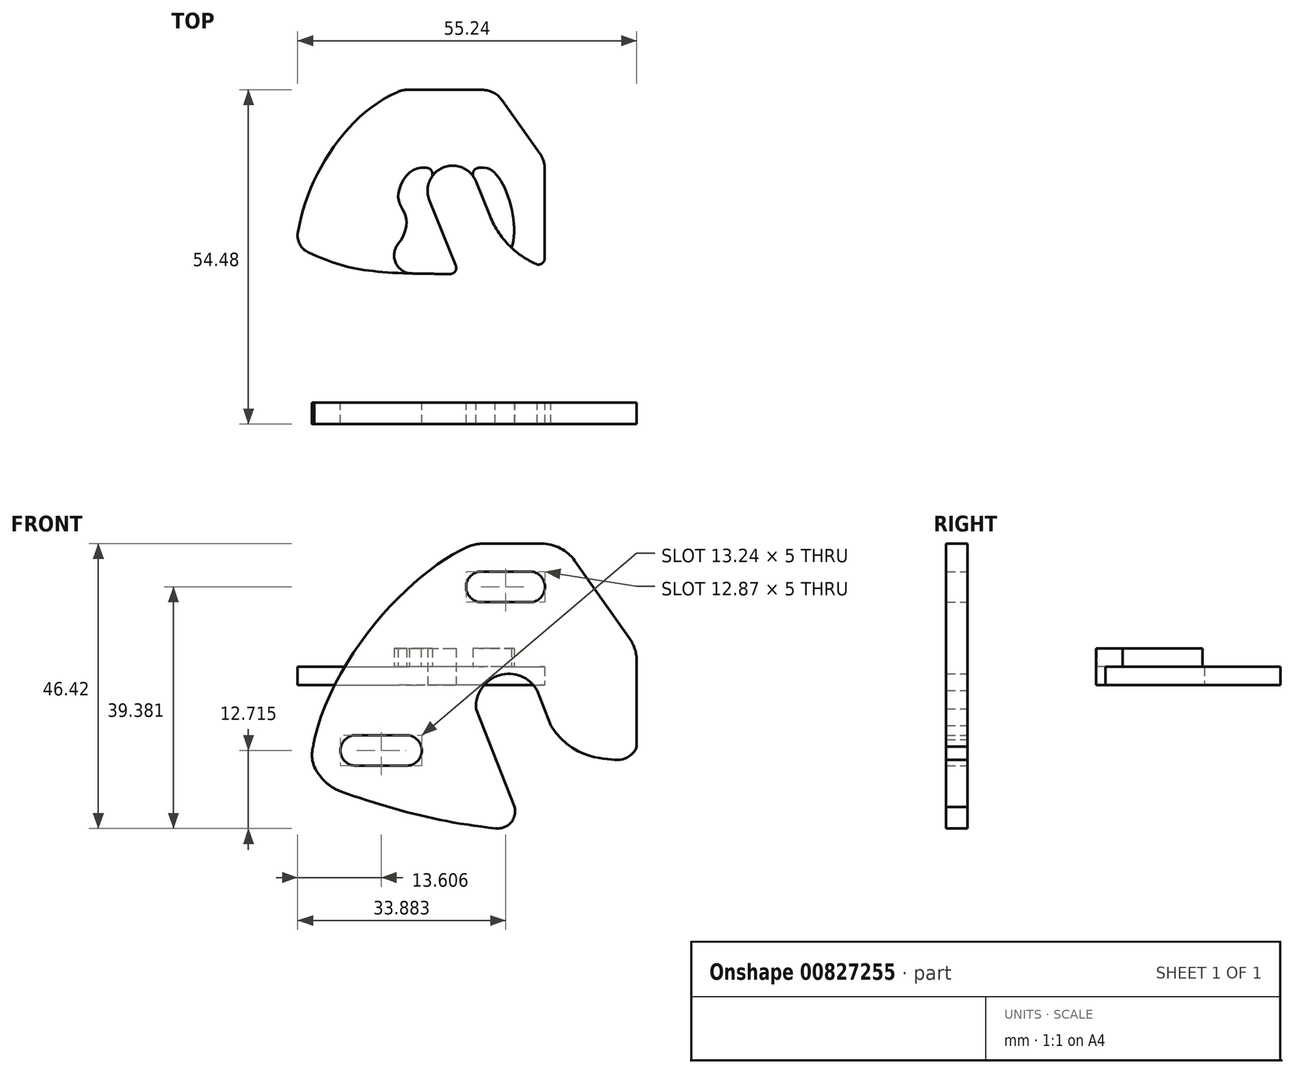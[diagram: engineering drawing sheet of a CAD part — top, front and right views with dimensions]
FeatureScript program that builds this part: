
annotation { "Feature Type Name" : "Feature", "Feature Type Description" : "" }
export const myFeature = defineFeature(function(context is Context, id is Id, definition is map)
    precondition{}
    {
        {
            var Q0;
            Q0=qCreatedBy(makeId("Top.planeOp"),FACE);
            var sketch = newSketch(context, id + "F0", { "sketchPlane" : qUnion([Q0])});
            skLineSegment(sketch, "E0", {"start": v(4.25, 49.3) * mm, "end": v(10.45, 40.56) * mm});
            skLineSegment(sketch, "E1", {"start": v(11.2, 22.02) * mm, "end": v(11.2, 38.24) * mm});
            skLineSegment(sketch, "E2", {"start": v(-7.58, 33) * mm, "end": v(-2.72, 20.95) * mm});
            skLineSegment(sketch, "E3", {"start": v(1, 50.98) * mm, "end": v(-11.14, 50.98) * mm});
            skLineSegment(sketch, "E4", {"start": v(2.27, 30.41) * mm, "end": v(0, 36.06) * mm});
            skFitSpline(sketch, "E5", {"points": [v(-29.3, 25.47) * mm, v(-11.94, 50.98) * mm], "startDerivative": vector(2.86, 30.39) * mm, "endDerivative": vector(29.4, 11.58) * mm});
            skFitSpline(sketch, "E6", {"points": [v(-29.3, 25.47) * mm, v(-2.72, 20.95) * mm], "startDerivative": vector(25.14, -12.86) * mm, "endDerivative": vector(43.82, -0.3) * mm});
            skArc(sketch, "E7", {"start": v(0, 36.06) * mm, "mid": v(-5.32, 38.32) * mm, "end": v(-7.58, 33) * mm});
            skArc(sketch, "E8", {"start": v(2.27, 30.41) * mm, "mid": v(5.81, 25.24) * mm, "end": v(11.2, 22.02) * mm});
            skLineSegment(sketch, "E9", {"start": v(-2.13, 38.26) * mm, "end": v(1.37, 38.26) * mm});
            skFitSpline(sketch, "E10", {"points": [v(5.81, 25.24) * mm, v(1.37, 38.26) * mm], "startDerivative": vector(4.46, 12.1) * mm, "endDerivative": vector(-9.6, 0) * mm});
            skLineSegment(sketch, "E11", {"start": v(-5.45, 38.26) * mm, "end": v(-8.94, 38.26) * mm});
            skFitSpline(sketch, "E12", {"points": [v(-8.94, 38.26) * mm, v(-12.66, 33.83) * mm, v(-11.42, 30.22) * mm, v(-12.66, 25.88) * mm], "startDerivative": vector(-14.89, 0.92) * mm, "endDerivative": vector(-9.91, -12.18) * mm});
            skArc(sketch, "E13", {"start": v(-12.66, 25.88) * mm, "mid": v(-12.95, 22.55) * mm, "end": v(-9.97, 21.04) * mm});
            skPoint(sketch, "E14.visualSharp", {"position": v(11.2, 39.52) * mm});
            skArc(sketch, "E14.filletArc", {"start": v(11.2, 38.24) * mm, "mid": v(11, 39.46) * mm, "end": v(10.45, 40.56) * mm});
            skPoint(sketch, "E15.visualSharp", {"position": v(3.06, 50.98) * mm});
            skArc(sketch, "E15.filletArc", {"start": v(4.25, 49.3) * mm, "mid": v(2.83, 50.53) * mm, "end": v(1, 50.98) * mm});
            skArc(sketch, "E16.filletArc", {"start": v(-11.14, 50.98) * mm, "mid": v(-11.97, 50.89) * mm, "end": v(-12.77, 50.63) * mm});
            skArc(sketch, "E17.filletArc", {"start": v(-29, 27.72) * mm, "mid": v(-28.71, 25.83) * mm, "end": v(-27.33, 24.5) * mm});
            skSolve(sketch);
        }
        {
            var Q0;
            Q0=makeQuery(id+"F0.imprint","IMPRINT",FACE,{"disambiguationData":[TD([[makeQuery(id+"F0.imprint","IMPRINT",EDGE,{"derivedFrom":sQuery(id+"F0.wireOp",EDGE,"E0")}),-1.0]])]});
            extrude(context, id + "F1", {"entities" : qUnion([Q0]), "depth" : 3 * mm, "offsetDistance" : 25 * mm});
        }
        {
            var Q0;
            {var subQ1=sQuery(id+"F0.wireOp",EDGE,"E2");Q0=makeQuery(id+"F0.imprint","IMPRINT",FACE,{"disambiguationData":[TD([[makeQuery(id+"F0.imprint","IMPRINT",EDGE,{"derivedFrom":subQ1}),-1.0]])]});}
            var Q1;
            {var subQ1=sQuery(id+"F0.wireOp",EDGE,"E4");Q1=makeQuery(id+"F0.imprint","IMPRINT",FACE,{"disambiguationData":[TD([[makeQuery(id+"F0.imprint","IMPRINT",EDGE,{"derivedFrom":subQ1}),-1.0]])]});}
            extrude(context, id + "F2", {"entities" : qUnion([Q0, Q1]), "operationType" : NewBodyOperationType.ADD, "depth" : 6 * mm, "offsetDistance" : 25 * mm});
        }
        {
            var Q0;
            Q0=makeQuery(id+"F2.opExtrude","SWEPT_EDGE",EDGE,{"disambiguationData":[OSD([sQuery(id+"F0.wireOp",EDGE,"E7"),sQuery(id+"F0.wireOp",EDGE,"E9")])]});
            var Q1;
            Q1=makeQuery(id+"F2.opExtrude","SWEPT_EDGE",EDGE,{"disambiguationData":[OSD([sQuery(id+"F0.wireOp",EDGE,"E7"),sQuery(id+"F0.wireOp",EDGE,"E11")])]});
            var Q2;
            Q2=makeQuery(id+"F1.opExtrude","SWEPT_EDGE",EDGE,{"disambiguationData":[OSD([sQuery(id+"F0.wireOp",EDGE,"E1"),sQuery(id+"F0.wireOp",EDGE,"E8")])]});
            var Q3;
            Q3=makeQuery(id+"F2.opExtrude","SWEPT_EDGE",EDGE,{"disambiguationData":[OSD([sQuery(id+"F0.wireOp",EDGE,"E2"),sQuery(id+"F0.wireOp",EDGE,"E6")])]});
            fillet(context, id + "F3", {"entities" : qUnion([Q0, Q1, Q2, Q3]), "radius" : 1 * mm, "tangentPropagation" : true, "allowEdgeOverflow" : false});
        }
        {
            var Q0;
            Q0=qCreatedBy(makeId("Front.planeOp"),FACE);
            var sketch = newSketch(context, id + "F4", { "sketchPlane" : qUnion([Q0])});
            skLineSegment(sketch, "E18", {"start": v(0, 23.06) * mm, "end": v(14.14, 23.06) * mm});
            skLineSegment(sketch, "E19", {"start": v(14.14, 23.06) * mm, "end": v(26.2, 6) * mm});
            skLineSegment(sketch, "E20", {"start": v(26.2, 6) * mm, "end": v(26.2, -10.04) * mm});
            skLineSegment(sketch, "E21", {"start": v(0.9, 18.52) * mm, "end": v(8.77, 18.52) * mm});
            skLineSegment(sketch, "E22", {"start": v(0.9, 13.52) * mm, "end": v(8.77, 13.52) * mm});
            skLineSegment(sketch, "E23", {"start": v(-19.56, -8.15) * mm, "end": v(-11.32, -8.15) * mm});
            skLineSegment(sketch, "E24", {"start": v(-19.56, -13.15) * mm, "end": v(-11.32, -13.15) * mm});
            skArc(sketch, "E25", {"start": v(-11.32, -8.15) * mm, "mid": v(-8.82, -10.65) * mm, "end": v(-11.32, -13.15) * mm});
            skArc(sketch, "E26", {"start": v(-19.56, -8.15) * mm, "mid": v(-22.06, -10.65) * mm, "end": v(-19.56, -13.15) * mm});
            skArc(sketch, "E27", {"start": v(8.77, 13.52) * mm, "mid": v(11.27, 16.02) * mm, "end": v(8.77, 18.52) * mm});
            skArc(sketch, "E28", {"start": v(0.9, 18.52) * mm, "mid": v(-1.6, 16.02) * mm, "end": v(0.9, 13.52) * mm});
            skArc(sketch, "E29", {"start": v(10, -0.85) * mm, "mid": v(3.8, 1.6) * mm, "end": v(0, -3.87) * mm});
            skLineSegment(sketch, "E30", {"start": v(10, -0.85) * mm, "end": v(12.21, -6.6) * mm});
            skLineSegment(sketch, "E31", {"start": v(0, -3.87) * mm, "end": v(6.29, -19.88) * mm});
            skFitSpline(sketch, "E32", {"points": [v(26.2, -10.04) * mm, v(24.33, -11.95) * mm, v(21.95, -12.1) * mm, v(12.21, -6.6) * mm], "startDerivative": vector(-2.64, -10.58) * mm, "endDerivative": vector(-18.84, 29.09) * mm});
            skFitSpline(sketch, "E33", {"points": [v(0, 23.06) * mm, v(-26.32, -8.89) * mm], "startDerivative": vector(-25.36, -8.61) * mm, "endDerivative": vector(-10.83, -45.83) * mm});
            skFitSpline(sketch, "E34", {"points": [v(-26.32, -8.89) * mm, v(-23.08, -16.94) * mm], "startDerivative": vector(-0.56, -5) * mm, "endDerivative": vector(15, -11.11) * mm});
            skFitSpline(sketch, "E35", {"points": [v(-23.08, -16.94) * mm, v(3.12, -23.32) * mm], "startDerivative": vector(25.34, -9.23) * mm, "endDerivative": vector(27.42, -2.73) * mm});
            skFitSpline(sketch, "E36", {"points": [v(3.12, -23.32) * mm, v(6.29, -19.88) * mm], "startDerivative": vector(5.54, -0.94) * mm, "endDerivative": vector(-1.6, 6.3) * mm});
            skSolve(sketch);
        }
        {
            var Q0;
            Q0=makeQuery(id+"F4.imprint","IMPRINT",FACE,{"disambiguationData":[TD([[makeQuery(id+"F4.imprint","IMPRINT",EDGE,{"derivedFrom":sQuery(id+"F4.wireOp",EDGE,"E18")}),-1.0]])]});
            extrude(context, id + "F5", {"entities" : qUnion([Q0]), "depth" : 3.5 * mm, "offsetDistance" : 25 * mm});
        }
        {
            var Q0;
            Q0=makeQuery(id+"F5.opExtrude","SWEPT_EDGE",EDGE,{"disambiguationData":[OSD([sQuery(id+"F4.wireOp",EDGE,"E18"),sQuery(id+"F4.wireOp",EDGE,"E33")])]});
            var Q1;
            Q1=makeQuery(id+"F5.opExtrude","SWEPT_EDGE",EDGE,{"disambiguationData":[OSD([sQuery(id+"F4.wireOp",EDGE,"E18"),sQuery(id+"F4.wireOp",EDGE,"E19")])]});
            var Q2;
            Q2=makeQuery(id+"F5.opExtrude","SWEPT_EDGE",EDGE,{"disambiguationData":[OSD([sQuery(id+"F4.wireOp",EDGE,"E19"),sQuery(id+"F4.wireOp",EDGE,"E20")])]});
            var Q3;
            Q3=makeQuery(id+"F5.opExtrude","SWEPT_EDGE",EDGE,{"disambiguationData":[OSD([sQuery(id+"F4.wireOp",EDGE,"E34"),sQuery(id+"F4.wireOp",EDGE,"E35")])]});
            fillet(context, id + "F6", {"entities" : qUnion([Q0, Q1, Q2, Q3]), "radius" : 6.6 * mm, "tangentPropagation" : true, "allowEdgeOverflow" : false});
        }
    });
